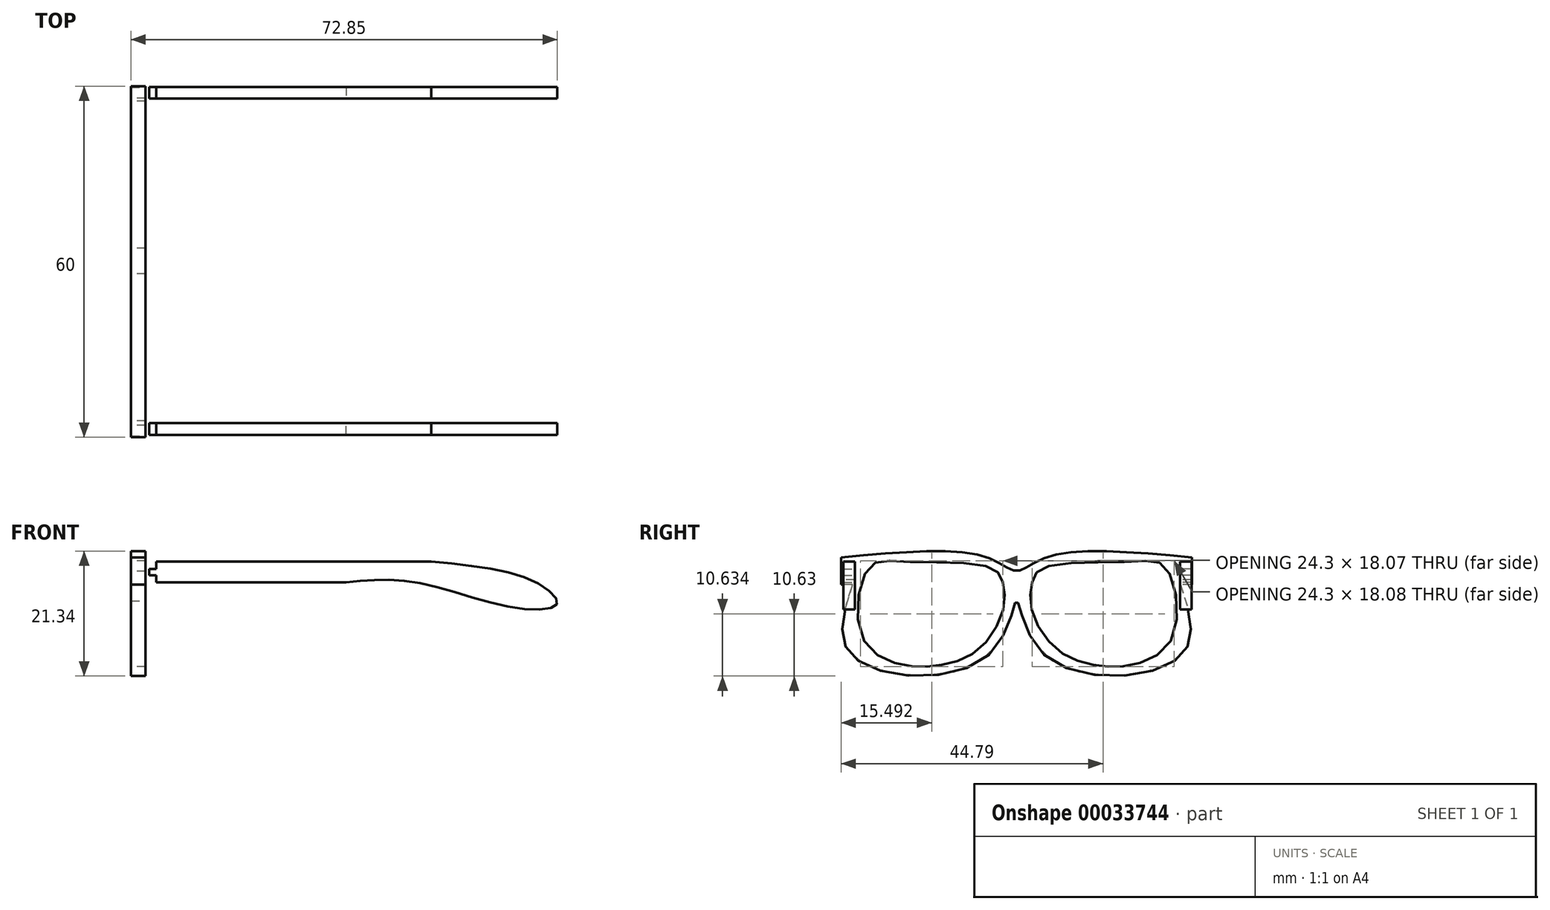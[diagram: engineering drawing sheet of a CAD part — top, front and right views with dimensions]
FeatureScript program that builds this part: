
annotation { "Feature Type Name" : "Feature", "Feature Type Description" : "" }
export const myFeature = defineFeature(function(context is Context, id is Id, definition is map)
    precondition{}
    {
        {
            var Q0;
            Q0=qCreatedBy(makeId("Front.planeOp"),FACE);
            var sketch = newSketch(context, id + "F0", { "sketchPlane" : qUnion([Q0])});
            skLineSegment(sketch, "E0", {"start": v(-30.17, 0) * mm, "end": v(-30.17, 1.2) * mm});
            skLineSegment(sketch, "E1", {"start": v(-30.17, 1.2) * mm, "end": v(-31.35, 1.2) * mm});
            skLineSegment(sketch, "E2", {"start": v(-31.35, 1.2) * mm, "end": v(-31.35, 2.3) * mm});
            skLineSegment(sketch, "E3", {"start": v(-31.35, 2.3) * mm, "end": v(-30.17, 2.3) * mm});
            skLineSegment(sketch, "E4", {"start": v(-30.17, 2.3) * mm, "end": v(-30.17, 3.57) * mm});
            skLineSegment(sketch, "E5", {"start": v(-30.17, 3.57) * mm, "end": v(16.84, 3.57) * mm});
            skLineSegment(sketch, "E6", {"start": v(-30.17, 0) * mm, "end": v(2.32, 0) * mm});
            skFitSpline(sketch, "E7", {"points": [v(16.84, 3.57) * mm, v(34.72, 0) * mm, v(38.32, -3.7) * mm, v(31, -4.33) * mm, v(14.06, 0) * mm, v(2.32, 0) * mm], "startDerivative": vector(80.04, -8.07) * mm, "endDerivative": vector(-54.78, -5.44) * mm});
            skSolve(sketch);
        }
        {
            var Q0;
            Q0=makeQuery(id+"F0.imprint","IMPRINT",FACE,{"disambiguationData":[TD([[makeQuery(id+"F0.imprint","IMPRINT",EDGE,{"derivedFrom":sQuery(id+"F0.wireOp",EDGE,"E0")}),-1.0]])]});
            extrude(context, id + "F1", {"entities" : qUnion([Q0]), "endBound" : BoundingType.SYMMETRIC, "depth" : 2 * mm});
        }
        {
            var Q0;
            Q0=makeQuery(id+"F1.opExtrude","SWEPT_BODY",BODY,{"disambiguationData":[OSD([sQuery(id+"F0.wireOp",EDGE,"E0"),sQuery(id+"F0.wireOp",EDGE,"E1"),sQuery(id+"F0.wireOp",EDGE,"E2"),sQuery(id+"F0.wireOp",EDGE,"E3"),sQuery(id+"F0.wireOp",EDGE,"E4"),sQuery(id+"F0.wireOp",EDGE,"E5"),sQuery(id+"F0.wireOp",EDGE,"E6"),sQuery(id+"F0.wireOp",EDGE,"E7")])]});
            var Q1;
            Q1=makeQuery(id+"F1.opExtrude","CAP_FACE",FACE,{"disambiguationData":[OSD([sQuery(id+"F0.wireOp",EDGE,"E0"),sQuery(id+"F0.wireOp",EDGE,"E1"),sQuery(id+"F0.wireOp",EDGE,"E2"),sQuery(id+"F0.wireOp",EDGE,"E3"),sQuery(id+"F0.wireOp",EDGE,"E4"),sQuery(id+"F0.wireOp",EDGE,"E5"),sQuery(id+"F0.wireOp",EDGE,"E6"),sQuery(id+"F0.wireOp",EDGE,"E7")])],"isStart":false});
            mirror(context, id + "F2", {"entities" : qUnion([Q0]), "mirrorPlane" : qUnion([Q1])});
        }
        {
            var Q0;
            Q0=makeQuery(id+"F2.opPattern","COPY",BODY,{"derivedFrom":makeQuery(id+"F1.opExtrude","SWEPT_BODY",BODY,{"disambiguationData":[OSD([sQuery(id+"F0.wireOp",EDGE,"E0"),sQuery(id+"F0.wireOp",EDGE,"E1"),sQuery(id+"F0.wireOp",EDGE,"E2"),sQuery(id+"F0.wireOp",EDGE,"E3"),sQuery(id+"F0.wireOp",EDGE,"E4"),sQuery(id+"F0.wireOp",EDGE,"E5"),sQuery(id+"F0.wireOp",EDGE,"E6"),sQuery(id+"F0.wireOp",EDGE,"E7")])]}),"instanceName":"1"});
            transform(context, id + "F3", {"entities" : qUnion([Q0]), "transformType" : TransformType.TRANSLATION_3D, "dx" : 0 * mm, "dy" : 50.13 * mm, "dz" : 0 * mm, "makeCopy" : false});
        }
        {
            var Q0;
            Q0=qCreatedBy(makeId("Right.planeOp"),FACE);
            var sketch = newSketch(context, id + "F4", { "sketchPlane" : qUnion([Q0])});
            skLineSegment(sketch, "E8", {"start": v(53.4, 28.28) * mm, "end": v(53.4, 23.62) * mm});
            skLineSegment(sketch, "E9", {"start": v(-6.6, 23.62) * mm, "end": v(-6.6, 28.28) * mm});
            skPoint(sketch, "E10", {"position": v(28.4, 28.28) * mm});
            skPoint(sketch, "E11", {"position": v(18.4, 28.28) * mm});
            skPoint(sketch, "E12.2.internal.snap0", {"position": v(53.4, 25.95) * mm});
            skFitSpline(sketch, "E12", {"points": [v(53.4, 28.28) * mm, v(28.4, 28.28) * mm, v(23.4, 25.95) * mm, v(18.4, 28.28) * mm, v(-6.6, 28.28) * mm], "startDerivative": vector(-87.84, 8.09) * mm, "endDerivative": vector(-87.84, -8.09) * mm});
            skPoint(sketch, "E13", {"position": v(51.4, 23.62) * mm});
            skPoint(sketch, "E14", {"position": v(-4.6, 23.62) * mm});
            skFitSpline(sketch, "E15", {"points": [v(51.4, 23.62) * mm, v(51.4, 11.38) * mm, v(28.4, 11.38) * mm, v(23.4, 20.85) * mm, v(18.4, 11.38) * mm, v(-4.6, 11.38) * mm, v(-4.6, 23.62) * mm], "startDerivative": vector(30.78, -92.04) * mm, "endDerivative": vector(30.78, 92.04) * mm});
            skLineSegment(sketch, "E16", {"start": v(53.4, 23.62) * mm, "end": v(51.4, 23.62) * mm});
            skLineSegment(sketch, "E17", {"start": v(-4.6, 23.62) * mm, "end": v(-6.6, 23.62) * mm});
            skSolve(sketch);
        }
        {
            var Q0;
            Q0=makeQuery(id+"F4.imprint","IMPRINT",FACE,{"disambiguationData":[TD([[makeQuery(id+"F4.imprint","IMPRINT",EDGE,{"derivedFrom":sQuery(id+"F4.wireOp",EDGE,"E8")}),-1.0]])]});
            extrude(context, id + "F5", {"entities" : qUnion([Q0]), "endBound" : BoundingType.SYMMETRIC, "depth" : 2.5 * mm});
        }
        {
            var Q0;
            Q0=makeQuery(id+"F5.opExtrude","SWEPT_BODY",BODY,{"disambiguationData":[OSD([sQuery(id+"F4.wireOp",EDGE,"E8"),sQuery(id+"F4.wireOp",EDGE,"E9"),sQuery(id+"F4.wireOp",EDGE,"E12"),sQuery(id+"F4.wireOp",EDGE,"E15"),sQuery(id+"F4.wireOp",EDGE,"E16"),sQuery(id+"F4.wireOp",EDGE,"E17")])]});
            transform(context, id + "F6", {"entities" : qUnion([Q0]), "transformType" : TransformType.TRANSLATION_3D, "dx" : -33.23 * mm, "dy" : -4.17 * mm, "dz" : -24.03 * mm, "makeCopy" : false});
        }
        {
            var Q0;
            Q0=makeQuery(id+"F1.opExtrude","SWEPT_BODY",BODY,{"disambiguationData":[OSD([sQuery(id+"F0.wireOp",EDGE,"E0"),sQuery(id+"F0.wireOp",EDGE,"E1"),sQuery(id+"F0.wireOp",EDGE,"E2"),sQuery(id+"F0.wireOp",EDGE,"E3"),sQuery(id+"F0.wireOp",EDGE,"E4"),sQuery(id+"F0.wireOp",EDGE,"E5"),sQuery(id+"F0.wireOp",EDGE,"E6"),sQuery(id+"F0.wireOp",EDGE,"E7")])]});
            transform(context, id + "F7", {"entities" : qUnion([Q0]), "transformType" : TransformType.TRANSLATION_3D, "dx" : 0 * mm, "dy" : -9.4 * mm, "dz" : 0 * mm, "makeCopy" : false});
        }
        {
            var Q0;
            Q0=qCreatedBy(makeId("Right.planeOp"),FACE);
            var sketch = newSketch(context, id + "F8", { "sketchPlane" : qUnion([Q0])});
            skPoint(sketch, "E18", {"position": v(19.36, -3.2) * mm});
            skPoint(sketch, "E19", {"position": v(19.23, 1.99) * mm});
            skPoint(sketch, "E20", {"position": v(19.36, 0) * mm});
            skPoint(sketch, "E21", {"position": v(16.86, 0) * mm});
            skPoint(sketch, "E22", {"position": v(21.86, 0) * mm});
            skPoint(sketch, "E23", {"position": v(16.86, -4.94) * mm});
            skPoint(sketch, "E24", {"position": v(21.86, -4.94) * mm});
            skPoint(sketch, "E25", {"position": v(14.86, 0) * mm});
            skPoint(sketch, "E26", {"position": v(23.86, 0) * mm});
            skPoint(sketch, "E27", {"position": v(14.86, 2.49) * mm});
            skPoint(sketch, "E28", {"position": v(23.86, 2.49) * mm});
            skPoint(sketch, "E29", {"position": v(0, 2.49) * mm});
            skPoint(sketch, "E30", {"position": v(38.72, 2.49) * mm});
            skPoint(sketch, "E31", {"position": v(-6, 2.49) * mm});
            skPoint(sketch, "E32", {"position": v(44.72, 2.49) * mm});
            skPoint(sketch, "E33", {"position": v(-7.14, -4.94) * mm});
            skPoint(sketch, "E34", {"position": v(45.86, -4.94) * mm});
            skPoint(sketch, "E35", {"position": v(-7.14, -9.44) * mm});
            skPoint(sketch, "E36", {"position": v(45.86, -9.44) * mm});
            skPoint(sketch, "E37", {"position": v(0, -14.17) * mm});
            skPoint(sketch, "E38", {"position": v(38.72, -14.17) * mm});
            skPoint(sketch, "E39", {"position": v(6, -14.17) * mm});
            skPoint(sketch, "E40", {"position": v(32.72, -14.17) * mm});
            skPoint(sketch, "E41", {"position": v(12.26, -11.85) * mm});
            skPoint(sketch, "E42", {"position": v(12.26, 0) * mm});
            skPoint(sketch, "E43", {"position": v(26.46, 0) * mm});
            skPoint(sketch, "E44", {"position": v(-6, 3.53) * mm});
            skPoint(sketch, "E45", {"position": v(-5.94, 3.53) * mm});
            skPoint(sketch, "E46", {"position": v(0, 3.53) * mm});
            skFitSpline(sketch, "E47", {"points": [v(16.86, -0.02) * mm, v(14.86, 2.49) * mm, v(0, 3.53) * mm, v(-6, 2.49) * mm, v(-7.14, -9.44) * mm, v(0, -14.17) * mm, v(6, -14.17) * mm, v(12.26, -11.85) * mm, v(16.86, -4.94) * mm, v(16.86, -0.02) * mm]});
            skPoint(sketch, "E48", {"position": v(12.26, -11.76) * mm});
            skPoint(sketch, "E49", {"position": v(38.72, 3.53) * mm});
            skPoint(sketch, "E50", {"position": v(26.46, -11.76) * mm});
            skFitSpline(sketch, "E51", {"points": [v(21.86, 0) * mm, v(23.86, 2.49) * mm, v(38.72, 3.53) * mm, v(44.72, 2.49) * mm, v(45.86, -9.44) * mm, v(38.72, -14.17) * mm, v(32.72, -14.17) * mm, v(26.46, -11.76) * mm, v(21.86, -4.94) * mm, v(21.86, 0) * mm]});
            skPoint(sketch, "E52", {"position": v(18.84, -4.06) * mm});
            skPoint(sketch, "E53", {"position": v(19.62, -4.06) * mm});
            skSolve(sketch);
        }
        {
            var Q0;
            Q0=makeQuery(id+"F8.imprint","IMPRINT",FACE,{"disambiguationData":[TD([[makeQuery(id+"F8.imprint","IMPRINT",EDGE,{"derivedFrom":sQuery(id+"F8.wireOp",EDGE,"E47")}),1.0]])]});
            var Q1;
            Q1=makeQuery(id+"F8.imprint","IMPRINT",FACE,{"disambiguationData":[TD([[makeQuery(id+"F8.imprint","IMPRINT",EDGE,{"derivedFrom":sQuery(id+"F8.wireOp",EDGE,"E51")}),-1.0]])]});
            extrude(context, id + "F9", {"entities" : qUnion([Q0, Q1]), "operationType" : NewBodyOperationType.REMOVE, "oppositeDirection" : true, "depth" : 72.6 * mm});
        }
    });
